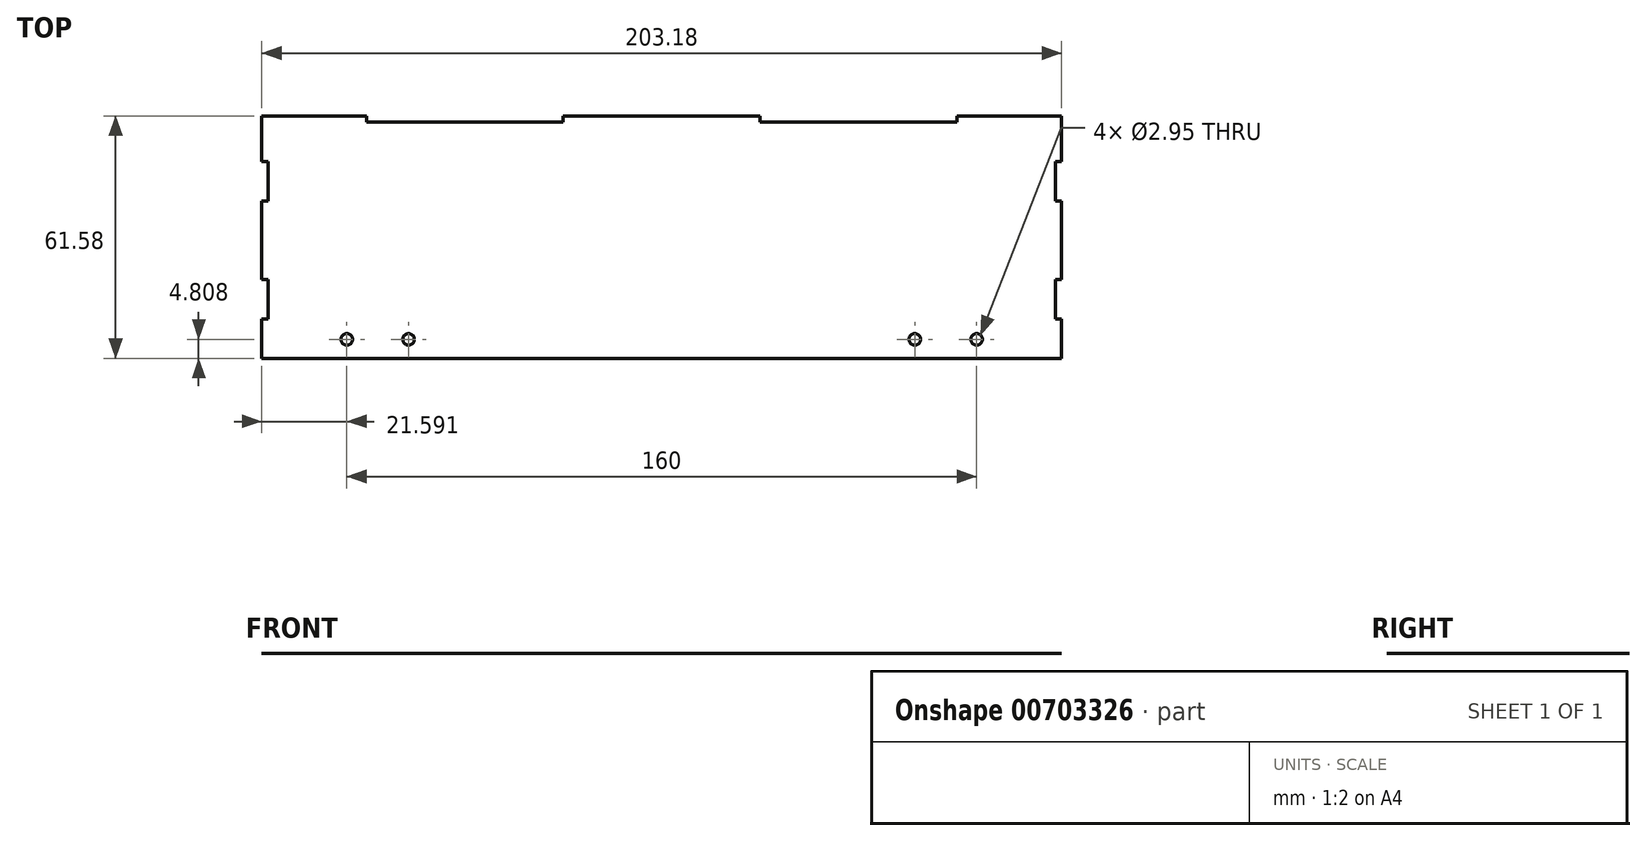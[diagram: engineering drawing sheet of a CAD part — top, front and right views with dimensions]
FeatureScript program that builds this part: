
annotation { "Feature Type Name" : "Feature", "Feature Type Description" : "" }
export const myFeature = defineFeature(function(context is Context, id is Id, definition is map)
    precondition{}
    {
        {
            var Q0;
            Q0=qCreatedBy(makeId("Top.planeOp"),FACE);
            var sketch = newSketch(context, id + "F0", { "sketchPlane" : qUnion([Q0])});
            skLineSegment(sketch, "E0.bottom", {"start": v(100.06, 18.89) * mm, "end": v(-99.94, 18.89) * mm});
            skLineSegment(sketch, "E0.top", {"start": v(100.06, -21.11) * mm, "end": v(-99.94, -21.11) * mm});
            skLineSegment(sketch, "E0.left", {"start": v(100.06, 18.89) * mm, "end": v(100.06, -21.11) * mm});
            skLineSegment(sketch, "E0.right", {"start": v(-99.94, 18.89) * mm, "end": v(-99.94, -21.11) * mm});
            skLineSegment(sketch, "E1", {"start": v(100.06, 18.89) * mm, "end": v(100.06, 28.89) * mm});
            skLineSegment(sketch, "E2", {"start": v(100.06, 28.89) * mm, "end": v(-99.94, 28.89) * mm});
            skLineSegment(sketch, "E3", {"start": v(-99.94, 28.89) * mm, "end": v(-99.94, 18.89) * mm});
            skLineSegment(sketch, "E4", {"start": v(-99.94, -21.11) * mm, "end": v(-99.94, -31.11) * mm});
            skLineSegment(sketch, "E5", {"start": v(-99.94, -31.11) * mm, "end": v(100.06, -31.11) * mm});
            skLineSegment(sketch, "E6", {"start": v(100.06, -31.11) * mm, "end": v(100.06, -21.11) * mm});
            skLineSegment(sketch, "E7", {"start": v(-99.94, 8.89) * mm, "end": v(-101.53, 8.89) * mm});
            skLineSegment(sketch, "E8", {"start": v(-101.53, 8.89) * mm, "end": v(-101.53, -11.11) * mm});
            skLineSegment(sketch, "E9", {"start": v(-101.53, -11.11) * mm, "end": v(-99.94, -11.11) * mm});
            skLineSegment(sketch, "E10", {"start": v(100.06, 8.89) * mm, "end": v(101.65, 8.89) * mm});
            skLineSegment(sketch, "E11", {"start": v(101.65, 8.89) * mm, "end": v(101.65, -11.11) * mm});
            skLineSegment(sketch, "E12", {"start": v(101.65, -11.11) * mm, "end": v(100.06, -11.11) * mm});
            skLineSegment(sketch, "E13", {"start": v(-99.94, 18.89) * mm, "end": v(-101.53, 18.89) * mm});
            skLineSegment(sketch, "E14", {"start": v(-101.53, 18.89) * mm, "end": v(-101.53, 28.89) * mm});
            skLineSegment(sketch, "E15", {"start": v(-101.53, 28.89) * mm, "end": v(-99.94, 28.89) * mm});
            skLineSegment(sketch, "E16", {"start": v(-99.94, -21.11) * mm, "end": v(-101.53, -21.11) * mm});
            skLineSegment(sketch, "E17", {"start": v(-101.53, -21.11) * mm, "end": v(-101.53, -31.11) * mm});
            skLineSegment(sketch, "E18", {"start": v(-101.53, -31.11) * mm, "end": v(-99.94, -31.11) * mm});
            skLineSegment(sketch, "E19", {"start": v(100.06, -21.11) * mm, "end": v(101.65, -21.11) * mm});
            skLineSegment(sketch, "E20", {"start": v(101.65, -21.11) * mm, "end": v(101.65, -31.11) * mm});
            skLineSegment(sketch, "E21", {"start": v(101.65, -31.11) * mm, "end": v(100.06, -31.11) * mm});
            skLineSegment(sketch, "E22", {"start": v(100.06, 28.89) * mm, "end": v(101.65, 28.89) * mm});
            skLineSegment(sketch, "E23", {"start": v(101.65, 28.89) * mm, "end": v(101.65, 18.89) * mm});
            skLineSegment(sketch, "E24", {"start": v(101.65, 18.89) * mm, "end": v(100.06, 18.89) * mm});
            skLineSegment(sketch, "E25", {"start": v(-101.53, 28.89) * mm, "end": v(-101.53, 30.47) * mm});
            skLineSegment(sketch, "E26", {"start": v(-101.53, 30.47) * mm, "end": v(101.65, 30.47) * mm});
            skLineSegment(sketch, "E27", {"start": v(101.65, 30.47) * mm, "end": v(101.65, 28.89) * mm});
            skLineSegment(sketch, "E28", {"start": v(101.65, -31.11) * mm, "end": v(101.65, -32.7) * mm});
            skLineSegment(sketch, "E29", {"start": v(101.65, -32.7) * mm, "end": v(-99.94, -32.7) * mm});
            skLineSegment(sketch, "E30", {"start": v(-99.94, -32.7) * mm, "end": v(-99.94, -31.11) * mm});
            skLineSegment(sketch, "E31", {"start": v(-74.94, 30.47) * mm, "end": v(-74.94, 28.89) * mm});
            skLineSegment(sketch, "E32", {"start": v(-24.94, 30.47) * mm, "end": v(-24.94, 28.89) * mm});
            skLineSegment(sketch, "E33", {"start": v(25.06, 30.47) * mm, "end": v(25.06, 28.89) * mm});
            skLineSegment(sketch, "E34", {"start": v(75.06, 30.47) * mm, "end": v(75.06, 28.89) * mm});
            skLineSegment(sketch, "E35", {"start": v(-101.53, -31.11) * mm, "end": v(-101.53, -32.7) * mm});
            skLineSegment(sketch, "E36", {"start": v(-101.53, -32.7) * mm, "end": v(-99.94, -32.7) * mm});
            skCircle(sketch, "E37", {"center": v(-79.94, -26.3) * mm, "radius": 1.47 * mm});
            skCircle(sketch, "E38", {"center": v(-64.24, -26.3) * mm, "radius": 1.47 * mm});
            skCircle(sketch, "E39", {"center": v(80.06, -26.3) * mm, "radius": 1.47 * mm});
            skCircle(sketch, "E40", {"center": v(64.36, -26.3) * mm, "radius": 1.47 * mm});
            skSolve(sketch);
        }
        {
            var Q0;
            {var subQ0=sQuery(id+"F0.wireOp",EDGE,"E10");Q0=makeQuery(id+"F0.imprint","IMPRINT",FACE,{"disambiguationData":[TD([[makeQuery(id+"F0.imprint","IMPRINT",EDGE,{"derivedFrom":subQ0}),-1.0]])]});}
            var Q1;
            {var subQ0=sQuery(id+"F0.wireOp",EDGE,"E7");Q1=makeQuery(id+"F0.imprint","IMPRINT",FACE,{"disambiguationData":[TD([[makeQuery(id+"F0.imprint","IMPRINT",EDGE,{"derivedFrom":subQ0}),1.0]])]});}
            var Q2;
            Q2=makeQuery(id+"F0.imprint","IMPRINT",FACE,{"disambiguationData":[TD([[makeQuery(id+"F0.imprint","IMPRINT",EDGE,{"derivedFrom":sQuery(id+"F0.wireOp",EDGE,"E4")}),-1.0]])]});
            var Q3;
            Q3=makeQuery(id+"F0.imprint","IMPRINT",FACE,{"disambiguationData":[TD([[makeQuery(id+"F0.imprint","IMPRINT",EDGE,{"derivedFrom":sQuery(id+"F0.wireOp",EDGE,"E1")}),-1.0]])]});
            var Q4;
            Q4=makeQuery(id+"F0.imprint","IMPRINT",FACE,{"disambiguationData":[TD([[makeQuery(id+"F0.imprint","IMPRINT",EDGE,{"derivedFrom":sQuery(id+"F0.wireOp",EDGE,"E3")}),-1.0]])]});
            var Q5;
            Q5=makeQuery(id+"F0.imprint","IMPRINT",FACE,{"disambiguationData":[TD([[makeQuery(id+"F0.imprint","IMPRINT",EDGE,{"derivedFrom":sQuery(id+"F0.wireOp",EDGE,"E6")}),-1.0]])]});
            var Q6;
            {var subQ1=sQuery(id+"F0.wireOp",EDGE,"E22");Q6=makeQuery(id+"F0.imprint","IMPRINT",FACE,{"disambiguationData":[TD([[makeQuery(id+"F0.imprint","IMPRINT",EDGE,{"derivedFrom":subQ1}),1.0]])]});}
            var Q7;
            {var subQ0=sQuery(id+"F0.wireOp",EDGE,"E32");Q7=makeQuery(id+"F0.imprint","IMPRINT",FACE,{"disambiguationData":[TD([[makeQuery(id+"F0.imprint","IMPRINT",EDGE,{"derivedFrom":subQ0}),1.0]])]});}
            var Q8;
            {var subQ3=sQuery(id+"F0.wireOp",EDGE,"E15");Q8=makeQuery(id+"F0.imprint","IMPRINT",FACE,{"disambiguationData":[TD([[makeQuery(id+"F0.imprint","IMPRINT",EDGE,{"derivedFrom":subQ3}),1.0]])]});}
            var Q9;
            {var subQ3=sQuery(id+"F0.wireOp",EDGE,"E0.bottom");Q9=makeQuery(id+"F0.imprint","IMPRINT",FACE,{"disambiguationData":[TD([[makeQuery(id+"F0.imprint","IMPRINT",EDGE,{"derivedFrom":subQ3}),1.0]])]});}
            var Q10;
            Q10=makeQuery(id+"F0.imprint","IMPRINT",FACE,{"disambiguationData":[TD([[makeQuery(id+"F0.imprint","IMPRINT",EDGE,{"derivedFrom":sQuery(id+"F0.wireOp",EDGE,"E0.top")}),1.0]])]});
            var Q11;
            Q11=makeQuery(id+"F0.imprint","IMPRINT",FACE,{"disambiguationData":[TD([[makeQuery(id+"F0.imprint","IMPRINT",EDGE,{"derivedFrom":sQuery(id+"F0.wireOp",EDGE,"E0.bottom")}),-1.0]])]});
            extrude(context, id + "F1", {"entities" : qUnion([Q0, Q1, Q2, Q3, Q4, Q5, Q6, Q7, Q8, Q9, Q10, Q11]), "depth" : 1 / 406.4 * mm, "offsetDistance" : 25 * mm});
        }
    });
